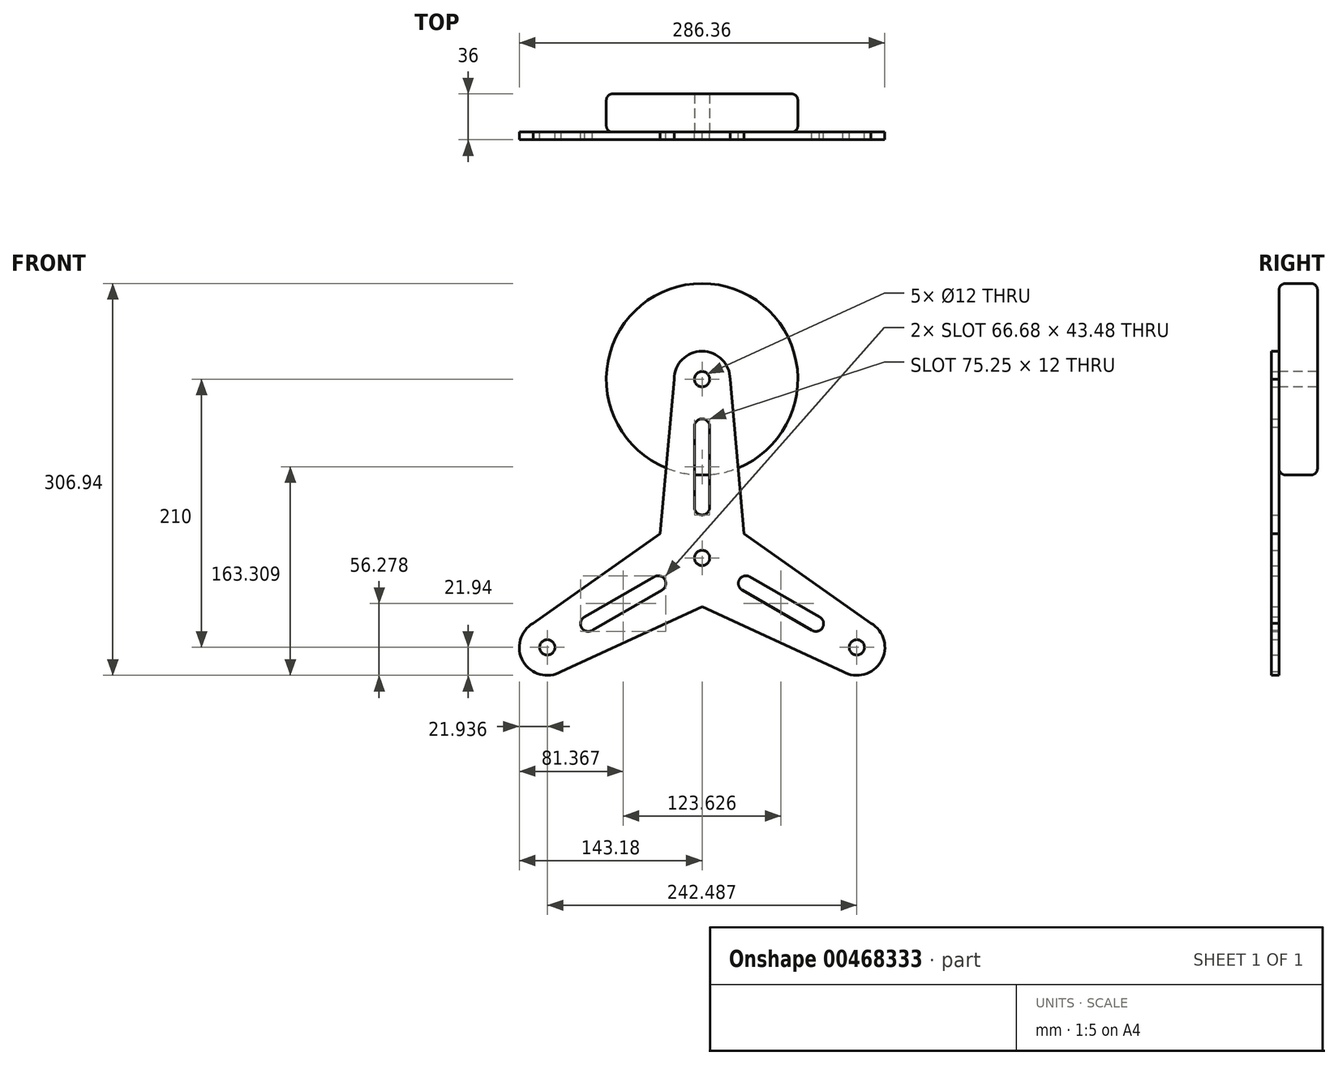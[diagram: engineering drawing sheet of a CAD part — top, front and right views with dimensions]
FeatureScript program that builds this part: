
annotation { "Feature Type Name" : "Feature", "Feature Type Description" : "" }
export const myFeature = defineFeature(function(context is Context, id is Id, definition is map)
    precondition{}
    {
        {
            var Q0;
            Q0=qCreatedBy(makeId("Front.planeOp"),FACE);
            var sketch = newSketch(context, id + "F0", { "sketchPlane" : qUnion([Q0])});
            skLineSegment(sketch, "E0", {"start": v(0, 0) * mm, "end": v(0, 140) * mm, "construction": true});
            skArc(sketch, "E1", {"start": v(21.94, 140) * mm, "mid": v(0, 161.94) * mm, "end": v(-21.94, 140) * mm});
            skLineSegment(sketch, "E2", {"start": v(0, 140) * mm, "end": v(-21.94, 140) * mm, "construction": true});
            skLineSegment(sketch, "E3", {"start": v(-21.94, 140) * mm, "end": v(-32.93, 19) * mm});
            skLineSegment(sketch, "E4.MirrorCS", {"start": v(21.94, 140) * mm, "end": v(32.93, 19) * mm});
            skLineSegment(sketch, "E5.1.0", {"start": v(-110.28, -89) * mm, "end": v(0, -38.02) * mm});
            skArc(sketch, "E5.1.1", {"start": v(-132.21, -51) * mm, "mid": v(-140.24, -80.97) * mm, "end": v(-110.28, -89) * mm});
            skLineSegment(sketch, "E5.1.2", {"start": v(-132.21, -51) * mm, "end": v(-32.93, 19) * mm});
            skLineSegment(sketch, "E5.2.0", {"start": v(132.21, -51) * mm, "end": v(32.93, 19) * mm});
            skArc(sketch, "E5.2.1", {"start": v(110.28, -89) * mm, "mid": v(140.24, -80.97) * mm, "end": v(132.21, -51) * mm});
            skLineSegment(sketch, "E5.2.2", {"start": v(110.28, -89) * mm, "end": v(0, -38.02) * mm});
            skPoint(sketch, "E5.center", {"position": v(0, 0) * mm});
            skPoint(sketch, "E6.orphan", {"position": v(-17.33, 30) * mm});
            skPoint(sketch, "E7.orphan", {"position": v(-34.65, 0) * mm});
            skPoint(sketch, "E8.orphan", {"position": v(-17.33, -30) * mm});
            skPoint(sketch, "E9.orphan", {"position": v(17.33, -30) * mm});
            skPoint(sketch, "E10.orphan", {"position": v(17.33, 30) * mm});
            skPoint(sketch, "E11.orphan", {"position": v(34.65, 0) * mm});
            skCircle(sketch, "E12", {"center": v(0, 0) * mm, "radius": 6 * mm});
            skCircle(sketch, "E13", {"center": v(0, 140) * mm, "radius": 6 * mm});
            skCircle(sketch, "E14", {"center": v(-121.24, -70) * mm, "radius": 6 * mm});
            skCircle(sketch, "E15", {"center": v(121.24, -70) * mm, "radius": 6 * mm});
            skArc(sketch, "E16", {"start": v(5.99, 102.6) * mm, "mid": v(0, 109) * mm, "end": v(-5.99, 102.6) * mm});
            skArc(sketch, "E17", {"start": v(-6, 39.75) * mm, "mid": v(0, 33.74) * mm, "end": v(6, 39.75) * mm});
            skLineSegment(sketch, "E18", {"start": v(-5.99, 103.38) * mm, "end": v(-6, 39.75) * mm});
            skLineSegment(sketch, "E19.MirrorCS", {"start": v(5.99, 103.38) * mm, "end": v(6, 39.75) * mm});
            skArc(sketch, "E20.1.0", {"start": v(-91.85, -46.12) * mm, "mid": v(-94.4, -54.5) * mm, "end": v(-85.86, -56.49) * mm});
            skLineSegment(sketch, "E20.1.1", {"start": v(-92.53, -46.5) * mm, "end": v(-37.42, -14.68) * mm});
            skLineSegment(sketch, "E20.1.2", {"start": v(-86.54, -56.88) * mm, "end": v(-31.42, -25.07) * mm});
            skArc(sketch, "E20.1.3", {"start": v(-31.42, -25.07) * mm, "mid": v(-29.22, -16.87) * mm, "end": v(-37.42, -14.68) * mm});
            skArc(sketch, "E20.2.0", {"start": v(85.86, -56.49) * mm, "mid": v(94.4, -54.5) * mm, "end": v(91.85, -46.12) * mm});
            skLineSegment(sketch, "E20.2.1", {"start": v(86.54, -56.88) * mm, "end": v(31.42, -25.07) * mm});
            skLineSegment(sketch, "E20.2.2", {"start": v(92.53, -46.5) * mm, "end": v(37.42, -14.68) * mm});
            skArc(sketch, "E20.2.3", {"start": v(37.42, -14.68) * mm, "mid": v(29.22, -16.87) * mm, "end": v(31.42, -25.07) * mm});
            skSolve(sketch);
        }
        {
            var Q0;
            Q0=makeQuery(id+"F0.imprint","IMPRINT",FACE,{"disambiguationData":[TD([[makeQuery(id+"F0.imprint","IMPRINT",EDGE,{"derivedFrom":sQuery(id+"F0.wireOp",EDGE,"E12")}),-1.0]])]});
            var Q1;
            {var subQ13=sQuery(id+"F0.wireOp",EDGE,"E5.1.1");Q1=makeQuery(id+"F0.imprint","IMPRINT",FACE,{"disambiguationData":[TD([[makeQuery(id+"F0.imprint","IMPRINT",EDGE,{"derivedFrom":subQ13}),1.0]])]});}
            var Q2;
            {var subQ12=sQuery(id+"F0.wireOp",EDGE,"E5.2.1");Q2=makeQuery(id+"F0.imprint","IMPRINT",FACE,{"disambiguationData":[TD([[makeQuery(id+"F0.imprint","IMPRINT",EDGE,{"derivedFrom":subQ12}),1.0]])]});}
            var Q3;
            {var subQ6=sQuery(id+"F0.wireOp",EDGE,"E1");Q3=makeQuery(id+"F0.imprint","IMPRINT",FACE,{"disambiguationData":[TD([[makeQuery(id+"F0.imprint","IMPRINT",EDGE,{"derivedFrom":subQ6}),1.0]])]});}
            extrude(context, id + "F1", {"entities" : qUnion([Q0, Q1, Q2, Q3]), "depth" : 6 * mm});
        }
        {
            var Q0;
            Q0=makeQuery(id+"F0.imprint","IMPRINT",FACE,{"disambiguationData":[TD([[makeQuery(id+"F0.imprint","IMPRINT",EDGE,{"derivedFrom":sQuery(id+"F0.wireOp",EDGE,"E13")}),1.0]])]});
            var sketch = newSketch(context, id + "F2", { "sketchPlane" : qUnion([Q0])});
            skCircle(sketch, "E21", {"center": v(0, 140) * mm, "radius": 75 * mm});
            skSolve(sketch);
        }
        {
            var Q0;
            Q0 = qSketchRegion(id + "F2", true);
            extrude(context, id + "F3", {"entities" : qUnion([Q0]), "oppositeDirection" : true, "depth" : 30 * mm});
        }
        {
            var Q0;
            Q0=makeQuery(id+"F3.opExtrude","CAP_EDGE",EDGE,{"disambiguationData":[OSD([sQuery(id+"F2.wireOp",EDGE,"E21")])],"isStart":true});
            var Q1;
            Q1=makeQuery(id+"F3.opExtrude","CAP_EDGE",EDGE,{"disambiguationData":[OSD([sQuery(id+"F2.wireOp",EDGE,"E21")])],"isStart":false});
            fillet(context, id + "F4", {"entities" : qUnion([Q0, Q1]), "radius" : 5 * mm, "tangentPropagation" : true, "allowEdgeOverflow" : false});
        }
        {
            var Q0;
            Q0=makeQuery(id+"F0.imprint","IMPRINT",FACE,{"disambiguationData":[TD([[makeQuery(id+"F0.imprint","IMPRINT",EDGE,{"derivedFrom":sQuery(id+"F0.wireOp",EDGE,"E13")}),1.0]])]});
            extrude(context, id + "F5", {"entities" : qUnion([Q0]), "operationType" : NewBodyOperationType.REMOVE, "endBound" : BoundingType.THROUGH_ALL, "oppositeDirection" : true, "depth" : 25 * mm});
        }
    });
